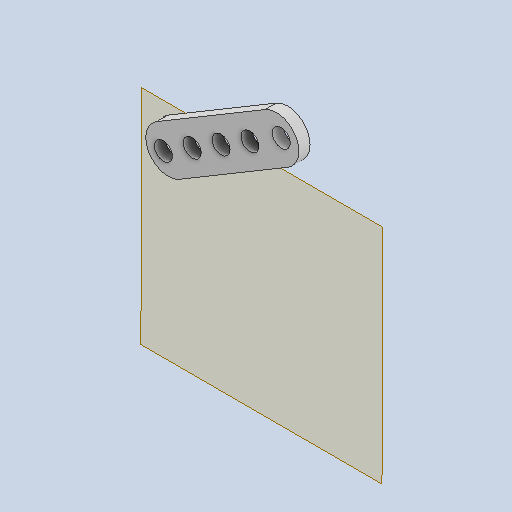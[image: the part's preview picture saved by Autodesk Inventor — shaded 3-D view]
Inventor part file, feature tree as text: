
AUTODESK INVENTOR PART (.ipt)
format: ipt  version: 2024.1 (Build 281209000, 209)  size: 168,960 bytes
history: native  units: mm
features: other x4, reference x2, plane x1, extrude x1, fillet x1, sketch x1
ambient origin geometry x8: Origin, YZ Plane, XZ Plane, XY Plane, X Axis, Y Axis, Z Axis, Center Point
bodies: Solid1 (feature_tree)
feature tree (10):
  plane  "Work Plane1"
  extrude  "Extrusion1"  Depth=8.0mm
  fillet  "Fillet1"  Radius=3.0mm
  sketch  "Sketch1"  dims[d0=4.0mm d1=8.0mm d2=3.0mm d3=3.0mm d4=4.0mm d5=40.0mm d7=6.0mm d8=10.0mm d10=10.0mm d12=2.0mm d13=0.0mm d14=4.0mm]
  reference  "Reference1"
  reference  "Reference2"
  other  "<userpath>\Documents\0004-CAD\3D-cad-main\the-artifact\artifact-assembly.iam"
  other  "artifact-assembly.iam"
  other  "control-arm:1"
  other  "leaf-lid:1"
